# Revit family: Faucet-Two_Handle-American_Standard-Colony_Pro-7074.55x_Series
name_source: partatom
category: Plumbing Fixtures
revit_build: Autodesk Revit 2018 (Build: 20170223_1515(x64)
units: mm (PartAtom-declared; Revit-internal decimal feet)

## family parameters
Always vertical = No
Cut with Voids When Loaded = No
OmniClass Number = 23.45.55.17
OmniClass Title = Mixing Faucets
Part Type = Normal
Room Calculation Point = No
Round Connector Dimension = Use Diameter
Shared = Yes
Work Plane-Based = Yes

## types (2) — shared parameters
ADA Compliant = Yes
Assembly Code = D2010310
CW Connection = Yes
CWFU = 1.5
Cold Water Connection Diameter = 1/2"
Cold Water Connection Radius = 1/4"
Default Elevation = 0"
Flow Rate = 1.5 gpm/5.7 L/min
HW Connection = Yes
HWFU = 1.5
Height = 12 1/2"
Hot Water Connection Diameter = 1"
Hot Water Connection Radius = 1/4"
IAPMO Compliance = ANSI A117.1, ASME A112.18.1, CSA B125.1, NSF 61/Section 9, NSF 372
Installation Type = Deck Mounted
Length = 10 3/8"
Manufacturer = American Standard
Material = Metal-American Standard-002-Polished Chrome
Price = Prices may vary. Please consult Manufacturer Representative for most up-to-date price list.
Product Documentation Link = https://www.americanstandard-us.com
Product Page URL = https://www.americanstandard-us.com
Revised Date = 03/26/2021
URL = http://www.americanstandard-us.com
Vent Connection = No
Warranty Information = Limited Lifetime Warranty
Waste Connection = No
Width = 7 11/16"
zero-valued in all types: WFU

## per-type parameters (varying)
| type | Description | Side-Spray |
| 7074.550 | The Colony PRO high-arc kitchen faucet from American Standard exemplifies fresh, transitional design with a durable, long-lasting construction that stands up to daily use even in the busiest of kitchens. A maximum flow rate of 1.5 gallons per minute helps to save water when compared to a standard 2.2 gpm faucet, without sacrificing performance – and our innovative quick-spin nuts make installation easy. | No |
| 7074.551 | The Colony Pro high-arc kitchen faucet from American Standard exemplifies fresh, transitional design with a durable, long-lasting construction that stands up to daily use even in the busiest of kitchens. Updating your kitchen is easy with the Colony Pro, available with a handy side-spray to help complete a wide variety of tasks. A maximum flow rate of 1.5 Gallons per minute helps to save water when , without sacrificing performance - and our innovative quick-spin nuts make installation easy. | Yes |

note: column(s) folded — value = type name in every type: Model

## geometry (parser evidence)
native form markers: Sweep x2
no freeform markers — native parametric forms only
